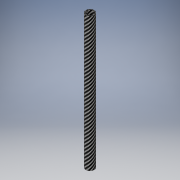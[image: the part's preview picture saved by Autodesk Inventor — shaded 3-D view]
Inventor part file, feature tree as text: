
AUTODESK INVENTOR PART (.ipt)
format: ipt  version: 2018 (Build 220112000, 112)  size: 112,128 bytes
history: native  units: in
note: dims shown in document units (in); Inventor stores cm internally (conversion verified against a paired STEP export)
features: extrude x1, sketch x1
ambient origin geometry x8: Origin, YZ Plane, XZ Plane, XY Plane, X Axis, Y Axis, Z Axis, Center Point
bodies: Solid1 (feature_tree)
feature tree (2):
  extrude  "Extrusion1"  Depth=5.9896in
  sketch  "Sketch1"  dims[d0=0.375in d1=0.31in d2=5.9896in d3=0.0in]
